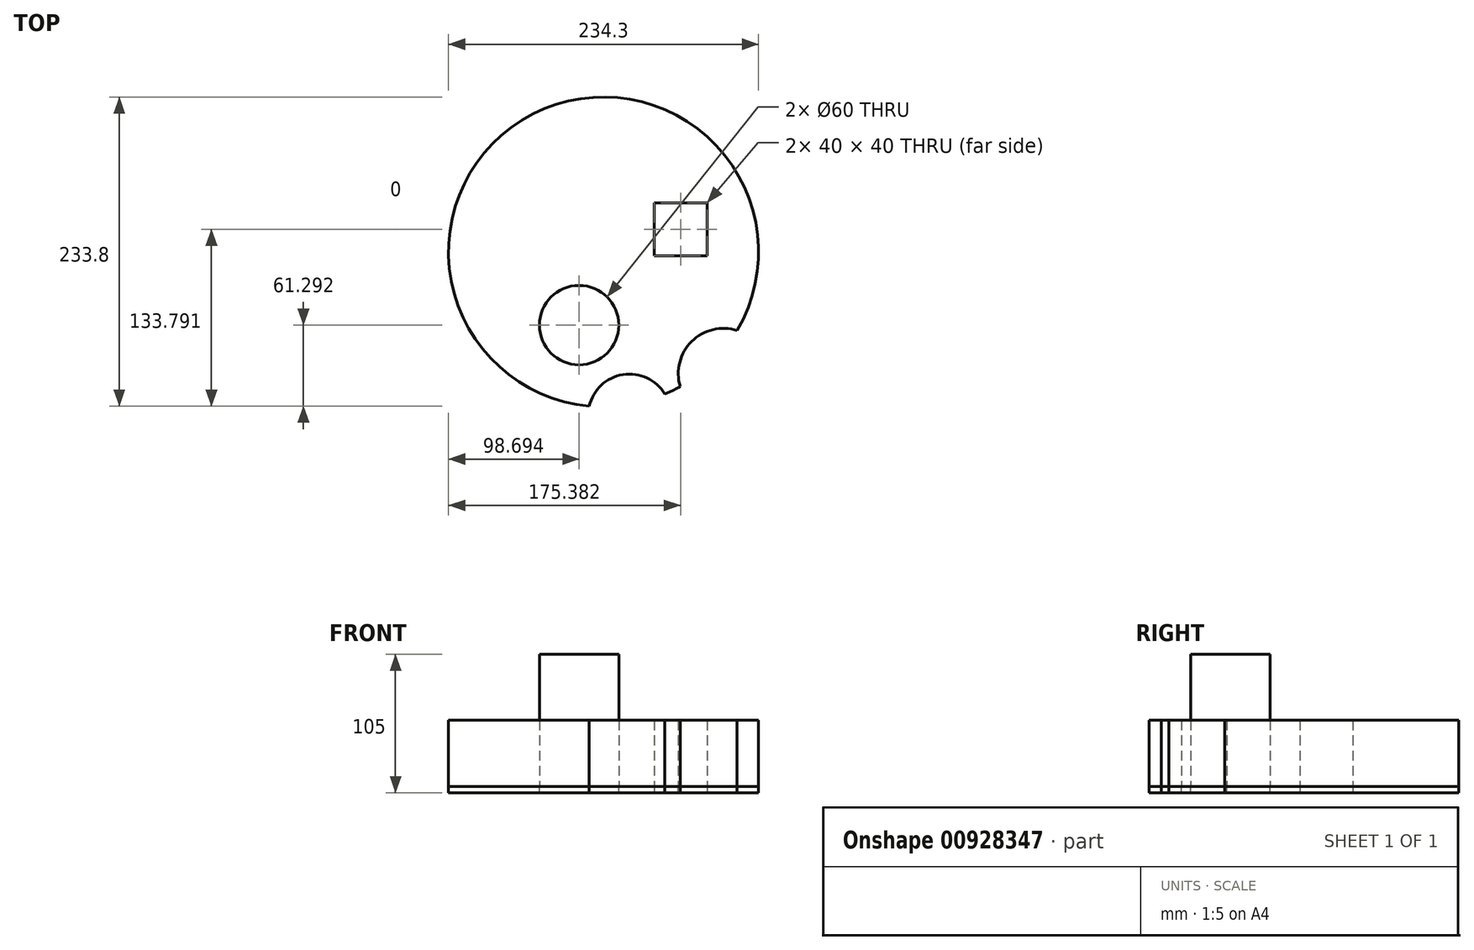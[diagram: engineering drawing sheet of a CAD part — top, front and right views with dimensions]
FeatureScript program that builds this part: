
annotation { "Feature Type Name" : "Feature", "Feature Type Description" : "" }
export const myFeature = defineFeature(function(context is Context, id is Id, definition is map)
    precondition{}
    {
        {
            var Q0;
            Q0=qCreatedBy(makeId("Top.planeOp"),FACE);
            var sketch = newSketch(context, id + "F0", { "sketchPlane" : qUnion([Q0])});
            skCircle(sketch, "E0", {"center": v(-82.24, -42.65) * mm, "radius": 34.11 * mm});
            skCircle(sketch, "E1", {"center": v(-153.2, -74.27) * mm, "radius": 31.2 * mm});
            skCircle(sketch, "E2", {"center": v(-191.3, -6.03) * mm, "radius": 30 * mm});
            skCircle(sketch, "E3", {"center": v(-172.84, 49.33) * mm, "radius": 117.15 * mm});
            skLineSegment(sketch, "E4.bottom", {"start": v(-31.7, 49.33) * mm, "end": v(31.7, 49.33) * mm});
            skLineSegment(sketch, "E4.top", {"start": v(-31.7, -49.33) * mm, "end": v(31.7, -49.33) * mm});
            skLineSegment(sketch, "E4.left", {"start": v(-31.7, 49.33) * mm, "end": v(-31.7, -49.33) * mm});
            skLineSegment(sketch, "E4.right", {"start": v(31.7, 49.33) * mm, "end": v(31.7, -49.33) * mm});
            skPoint(sketch, "E4.middle", {"position": v(0, 0) * mm});
            skLineSegment(sketch, "E5.bottom", {"start": v(-70.25, -25.71) * mm, "end": v(-94.23, -25.71) * mm});
            skLineSegment(sketch, "E5.top", {"start": v(-70.25, -59.59) * mm, "end": v(-94.23, -59.59) * mm});
            skLineSegment(sketch, "E5.left", {"start": v(-70.25, -25.71) * mm, "end": v(-70.25, -59.59) * mm});
            skLineSegment(sketch, "E5.right", {"start": v(-94.23, -25.71) * mm, "end": v(-94.23, -59.59) * mm});
            skSolve(sketch);
        }
        {
            var Q0;
            Q0=makeQuery(id+"F0.imprint","IMPRINT",FACE,{"disambiguationData":[TD([[makeQuery(id+"F0.imprint","IMPRINT",EDGE,{"derivedFrom":sQuery(id+"F0.wireOp",EDGE,"E2")}),-1.0]])]});
            extrude(context, id + "F1", {"entities" : qUnion([Q0]), "depth" : 50 * mm, "offsetDistance" : 25 * mm});
        }
        {
            var Q0;
            Q0=makeQuery(id+"F1.opExtrude","CAP_FACE",FACE,{"disambiguationData":[OSD([sQuery(id+"F0.wireOp",EDGE,"E0"),sQuery(id+"F0.wireOp",EDGE,"E1"),sQuery(id+"F0.wireOp",EDGE,"E2"),sQuery(id+"F0.wireOp",EDGE,"E3")])],"isStart":true});
            extrude(context, id + "F2", {"entities" : qUnion([Q0]), "depth" : 5 * mm, "offsetDistance" : 25 * mm});
        }
        {
            var Q0;
            Q0=makeQuery(id+"F2.opExtrude","CAP_FACE",FACE,{"disambiguationData":[OSD([sQuery(id+"F0.wireOp",EDGE,"E0"),sQuery(id+"F0.wireOp",EDGE,"E1"),sQuery(id+"F0.wireOp",EDGE,"E2"),sQuery(id+"F0.wireOp",EDGE,"E3")])],"isStart":false});
            var sketch = newSketch(context, id + "F3", { "sketchPlane" : qUnion([Q0])});
            skLineSegment(sketch, "E6.bottom", {"start": v(-134.6, -46.47) * mm, "end": v(-94.6, -46.47) * mm});
            skLineSegment(sketch, "E6.top", {"start": v(-134.6, -86.47) * mm, "end": v(-94.6, -86.47) * mm});
            skLineSegment(sketch, "E6.left", {"start": v(-134.6, -46.47) * mm, "end": v(-134.6, -86.47) * mm});
            skLineSegment(sketch, "E6.right", {"start": v(-94.6, -46.47) * mm, "end": v(-94.6, -86.47) * mm});
            skPoint(sketch, "E6.middle", {"position": v(-114.6, -66.47) * mm});
            skSolve(sketch);
        }
        {
            var Q0;
            Q0=makeQuery(id+"F0.imprint","IMPRINT",FACE,{"disambiguationData":[TD([[makeQuery(id+"F0.imprint","IMPRINT",EDGE,{"derivedFrom":sQuery(id+"F0.wireOp",EDGE,"E2")}),1.0]])]});
            extrude(context, id + "F4", {"entities" : qUnion([Q0]), "depth" : 100 * mm, "offsetDistance" : 25 * mm});
        }
        {
            var Q0;
            Q0=makeQuery(id+"F3.imprint","IMPRINT",FACE,{"disambiguationData":[TD([[makeQuery(id+"F3.imprint","IMPRINT",EDGE,{"derivedFrom":sQuery(id+"F3.wireOp",EDGE,"E6.bottom")}),-1.0]])]});
            extrude(context, id + "F5", {"entities" : qUnion([Q0]), "operationType" : NewBodyOperationType.REMOVE, "endBound" : BoundingType.THROUGH_ALL, "oppositeDirection" : true, "depth" : 25 * mm, "offsetDistance" : 25 * mm});
        }
    });
